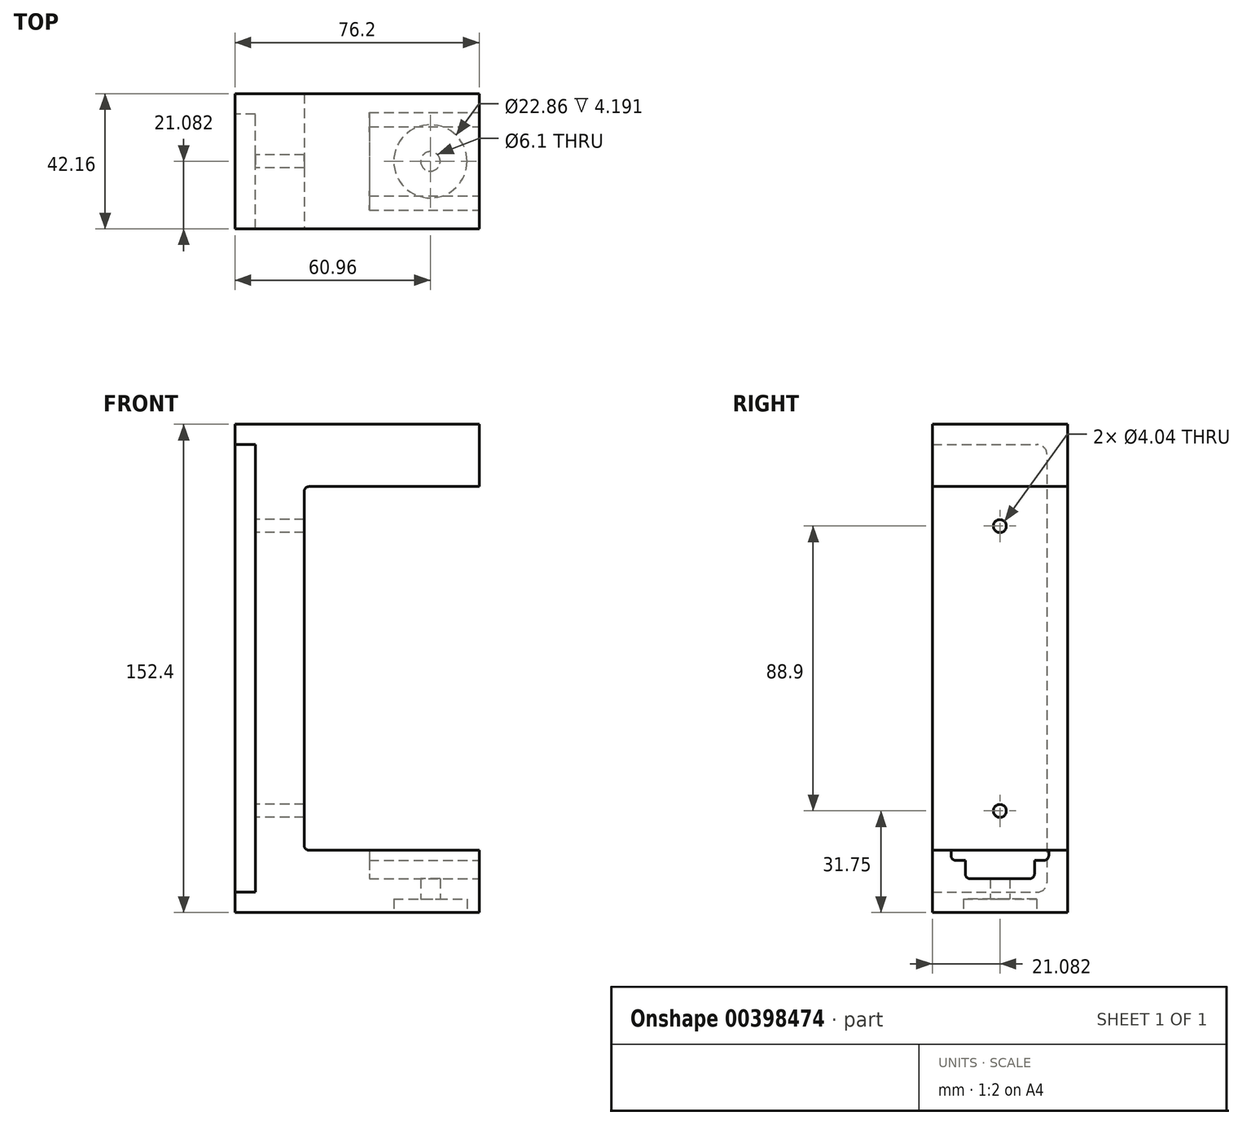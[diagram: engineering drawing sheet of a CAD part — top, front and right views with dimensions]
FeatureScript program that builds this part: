
annotation { "Feature Type Name" : "Feature", "Feature Type Description" : "" }
export const myFeature = defineFeature(function(context is Context, id is Id, definition is map)
    precondition{}
    {
        {
            var Q0;
            Q0=qCreatedBy(makeId("Top.planeOp"),FACE);
            var sketch = newSketch(context, id + "F0", { "sketchPlane" : qUnion([Q0])});
            skLineSegment(sketch, "E0.bottom", {"start": v(0, 0) * mm, "end": v(76.2, 0) * mm});
            skLineSegment(sketch, "E0.top", {"start": v(0, 42.16) * mm, "end": v(76.2, 42.16) * mm});
            skLineSegment(sketch, "E0.left", {"start": v(0, 0) * mm, "end": v(0, 42.16) * mm});
            skLineSegment(sketch, "E0.right", {"start": v(76.2, 0) * mm, "end": v(76.2, 42.16) * mm});
            skSolve(sketch);
        }
        {
            var Q0;
            Q0 = qSketchRegion(id + "F0", true);
            extrude(context, id + "F1", {"entities" : qUnion([Q0]), "depth" : 152.4 * mm});
        }
        {
            var Q0;
            Q0=makeQuery(id+"F1.opExtrude","SWEPT_FACE",FACE,{"disambiguationData":[OSD([sQuery(id+"F0.wireOp",EDGE,"E0.bottom")])]});
            var sketch = newSketch(context, id + "F2", { "sketchPlane" : qUnion([Q0])});
            skLineSegment(sketch, "E1", {"start": v(76.2, 19.43) * mm, "end": v(23.18, 19.43) * mm});
            skLineSegment(sketch, "E2", {"start": v(21.59, 21.02) * mm, "end": v(21.59, 131.38) * mm});
            skLineSegment(sketch, "E3", {"start": v(23.18, 132.97) * mm, "end": v(76.2, 132.97) * mm});
            skLineSegment(sketch, "E4", {"start": v(76.2, 132.97) * mm, "end": v(76.2, 19.43) * mm});
            skPoint(sketch, "E5.visualSharp", {"position": v(21.59, 19.43) * mm});
            skArc(sketch, "E5.filletArc", {"start": v(21.59, 21.02) * mm, "mid": v(22.05, 19.9) * mm, "end": v(23.18, 19.43) * mm});
            skPoint(sketch, "E6.visualSharp", {"position": v(21.59, 132.97) * mm});
            skArc(sketch, "E6.filletArc", {"start": v(23.18, 132.97) * mm, "mid": v(22.05, 132.5) * mm, "end": v(21.59, 131.38) * mm});
            skSolve(sketch);
        }
        {
            var Q0;
            Q0 = qSketchRegion(id + "F2", true);
            extrude(context, id + "F3", {"entities" : qUnion([Q0]), "operationType" : NewBodyOperationType.REMOVE, "endBound" : BoundingType.THROUGH_ALL, "oppositeDirection" : true, "depth" : 25.4 * mm});
        }
        {
            var Q0;
            {var subQ1=sQuery(id+"F0.wireOp",EDGE,"E0.right");Q0=makeQuery(id+"F3.boolean.opBoolean","SPLIT",FACE,{"disambiguationData":[TD([makeQuery(id+"F3.opExtrude","SWEPT_FACE",FACE,{"disambiguationData":[OSD([sQuery(id+"F2.wireOp",EDGE,"E1")])]})])],"derivedFrom":makeQuery(id+"F1.opExtrude","SWEPT_FACE",FACE,{"disambiguationData":[OSD([subQ1])]})});}
            var sketch = newSketch(context, id + "F4", { "sketchPlane" : qUnion([Q0])});
            skLineSegment(sketch, "E7.bottom", {"start": v(36.32, 19.43) * mm, "end": v(5.84, 19.43) * mm});
            skLineSegment(sketch, "E7.top", {"start": v(34.73, 16.26) * mm, "end": v(31.88, 16.26) * mm});
            skLineSegment(sketch, "E7.left", {"start": v(36.32, 19.43) * mm, "end": v(36.32, 17.84) * mm});
            skLineSegment(sketch, "E7.right", {"start": v(5.84, 19.43) * mm, "end": v(5.84, 17.84) * mm});
            skPoint(sketch, "E8.visualSharp", {"position": v(36.32, 16.26) * mm});
            skArc(sketch, "E8.filletArc", {"start": v(34.73, 16.26) * mm, "mid": v(35.86, 16.72) * mm, "end": v(36.32, 17.84) * mm});
            skPoint(sketch, "E9.visualSharp", {"position": v(5.84, 16.26) * mm});
            skArc(sketch, "E9.filletArc", {"start": v(5.84, 17.84) * mm, "mid": v(6.3, 16.72) * mm, "end": v(7.43, 16.26) * mm});
            skLineSegment(sketch, "E10.top", {"start": v(30.29, 10.54) * mm, "end": v(11.87, 10.54) * mm});
            skLineSegment(sketch, "E10.left", {"start": v(31.88, 16.26) * mm, "end": v(31.88, 12.13) * mm});
            skLineSegment(sketch, "E10.right", {"start": v(10.29, 16.26) * mm, "end": v(10.29, 12.13) * mm});
            skPoint(sketch, "E11.visualSharp", {"position": v(31.88, 10.54) * mm});
            skArc(sketch, "E11.filletArc", {"start": v(30.29, 10.54) * mm, "mid": v(31.41, 11) * mm, "end": v(31.88, 12.13) * mm});
            skPoint(sketch, "E12.visualSharp", {"position": v(10.29, 10.54) * mm});
            skArc(sketch, "E12.filletArc", {"start": v(10.29, 12.13) * mm, "mid": v(10.75, 11) * mm, "end": v(11.87, 10.54) * mm});
            skLineSegment(sketch, "E13.trimOffspring", {"start": v(10.29, 16.26) * mm, "end": v(7.43, 16.26) * mm});
            skSolve(sketch);
        }
        {
            var Q0;
            Q0 = qSketchRegion(id + "F4", true);
            extrude(context, id + "F5", {"entities" : qUnion([Q0]), "operationType" : NewBodyOperationType.REMOVE, "oppositeDirection" : true, "depth" : 34.3 * mm});
        }
        {
            var Q0;
            Q0=qCreatedBy(makeId("Top.planeOp"),FACE);
            cPlane(context, id + "F6", {"entities" : qUnion([Q0]), "cplaneType" : CPlaneType.OFFSET, "offset" : 76.2 * mm, "width" : 152.4 * mm, "height" : 152.4 * mm});
        }
        {
            var Q0;
            Q0=makeQuery(id+"F1.opExtrude","CAP_FACE",FACE,{"disambiguationData":[OSD([sQuery(id+"F0.wireOp",EDGE,"E0.bottom"),sQuery(id+"F0.wireOp",EDGE,"E0.top"),sQuery(id+"F0.wireOp",EDGE,"E0.left"),sQuery(id+"F0.wireOp",EDGE,"E0.right")])],"isStart":true});
            var sketch = newSketch(context, id + "F7", { "sketchPlane" : qUnion([Q0])});
            skCircle(sketch, "E14", {"center": v(60.96, -21.08) * mm, "radius": 11.43 * mm});
            skLineSegment(sketch, "E15", {"start": v(76.2, -21.08) * mm, "end": v(60.96, -21.08) * mm, "construction": true});
            skLineSegment(sketch, "E16", {"start": v(60.96, -21.08) * mm, "end": v(60.96, -42.16) * mm, "construction": true});
            skSolve(sketch);
        }
        {
            var Q0;
            Q0 = qSketchRegion(id + "F7", true);
            extrude(context, id + "F8", {"entities" : qUnion([Q0]), "operationType" : NewBodyOperationType.REMOVE, "oppositeDirection" : true, "depth" : 4.2 * mm});
        }
        {
            var Q0;
            Q0=makeQuery(id+"F8.boolean.opBoolean","COPY",FACE,{"derivedFrom":makeQuery(id+"F8.opExtrude","CAP_FACE",FACE,{"disambiguationData":[OSD([sQuery(id+"F7.wireOp",EDGE,"E14")])],"isStart":false})});
            var sketch = newSketch(context, id + "F9", { "sketchPlane" : qUnion([Q0])});
            skCircle(sketch, "E17", {"center": v(60.96, -21.08) * mm, "radius": 3.05 * mm});
            skSolve(sketch);
        }
        {
            var Q0;
            Q0 = qSketchRegion(id + "F9", true);
            extrude(context, id + "F10", {"entities" : qUnion([Q0]), "operationType" : NewBodyOperationType.REMOVE, "endBound" : BoundingType.UP_TO_NEXT, "oppositeDirection" : true, "depth" : 25.4 * mm});
        }
        {
            var Q0;
            Q0=makeQuery(id+"F1.opExtrude","SWEPT_FACE",FACE,{"disambiguationData":[OSD([sQuery(id+"F0.wireOp",EDGE,"E0.left")])]});
            var sketch = newSketch(context, id + "F11", { "sketchPlane" : qUnion([Q0])});
            skLineSegment(sketch, "E18.bottom", {"start": v(0, 6.35) * mm, "end": v(-32.64, 6.35) * mm});
            skLineSegment(sketch, "E18.top", {"start": v(0, 146.05) * mm, "end": v(-32.64, 146.05) * mm});
            skLineSegment(sketch, "E18.left", {"start": v(0, 6.35) * mm, "end": v(0, 146.05) * mm});
            skLineSegment(sketch, "E18.right", {"start": v(-35.81, 9.52) * mm, "end": v(-35.81, 142.88) * mm});
            skPoint(sketch, "E19.visualSharp", {"position": v(-35.81, 6.35) * mm});
            skArc(sketch, "E19.filletArc", {"start": v(-35.81, 9.52) * mm, "mid": v(-34.88, 7.28) * mm, "end": v(-32.64, 6.35) * mm});
            skPoint(sketch, "E20.visualSharp", {"position": v(-35.81, 146.05) * mm});
            skArc(sketch, "E20.filletArc", {"start": v(-32.64, 146.05) * mm, "mid": v(-34.88, 145.12) * mm, "end": v(-35.81, 142.88) * mm});
            skSolve(sketch);
        }
        {
            var Q0;
            Q0 = qSketchRegion(id + "F11", true);
            extrude(context, id + "F12", {"entities" : qUnion([Q0]), "operationType" : NewBodyOperationType.REMOVE, "oppositeDirection" : true, "depth" : 6.35 * mm});
        }
        {
            var Q0;
            Q0=makeQuery(id+"F12.boolean.opBoolean","COPY",FACE,{"derivedFrom":makeQuery(id+"F12.opExtrude","CAP_FACE",FACE,{"disambiguationData":[OSD([sQuery(id+"F11.wireOp",EDGE,"E18.bottom"),sQuery(id+"F11.wireOp",EDGE,"E18.top"),sQuery(id+"F11.wireOp",EDGE,"E18.left"),sQuery(id+"F11.wireOp",EDGE,"E18.right"),sQuery(id+"F11.wireOp",EDGE,"E19.filletArc"),sQuery(id+"F11.wireOp",EDGE,"E20.filletArc")])],"isStart":false})});
            var sketch = newSketch(context, id + "F13", { "sketchPlane" : qUnion([Q0])});
            skLineSegment(sketch, "E21", {"start": v(-21.08, 146.05) * mm, "end": v(-21.08, 6.35) * mm, "construction": true});
            skPoint(sketch, "E22", {"position": v(-21.08, 120.65) * mm});
            skPoint(sketch, "E23", {"position": v(-21.08, 31.75) * mm});
            skSolve(sketch);
        }
        {
            var Q0;
            Q0=sQuery(id+"F13.wireOp",VERTEX,"E22");
            var Q1;
            Q1=sQuery(id+"F13.wireOp",VERTEX,"E23");
            var Q2;
            Q2=makeQuery(id+"F1.opExtrude","SWEPT_BODY",BODY,{"disambiguationData":[OSD([sQuery(id+"F0.wireOp",EDGE,"E0.bottom"),sQuery(id+"F0.wireOp",EDGE,"E0.top"),sQuery(id+"F0.wireOp",EDGE,"E0.left"),sQuery(id+"F0.wireOp",EDGE,"E0.right")])]});
            hole(context, id + "F14", {"style" : HoleStyle.SIMPLE, "endStyle" : HoleEndStyle.THROUGH, "standardTappedOrClearance" : lookupTablePath({ "standard" : "ANSI", "engagement" : "75%", "pitch" : "32 tpi", "size" : "#10", "type" : "Tapped" }), "standardBlindInLast" : lookupTablePath({ "standard" : "ANSI", "engagement" : "75%", "pitch" : "32 tpi", "size" : "#10", "type" : "Tapped" }), "holeDiameter" : 4.04 * mm, "showTappedDepth" : true, "isTappedThrough" : true, "tappedDepth" : 12.7 * mm, "tapClearance" : 3, "locations" : qUnion([Q0, Q1]), "scope" : qUnion([Q2]), "majorDiameter" : 4.83 * mm});
        }
    });
